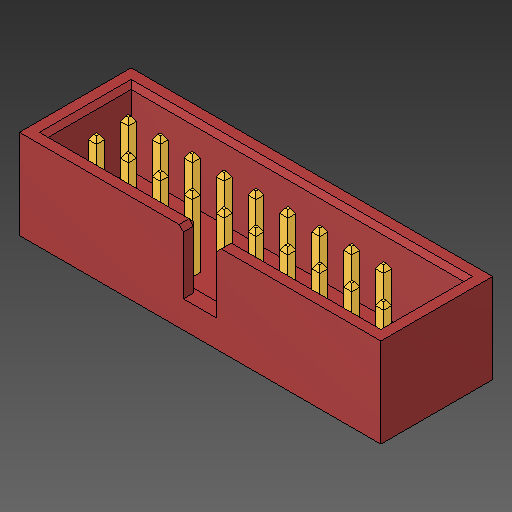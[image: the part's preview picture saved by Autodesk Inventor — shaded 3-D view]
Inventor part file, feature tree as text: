
AUTODESK INVENTOR PART (.ipt)
format: ipt  version: 2018.2 (Build 222227000, 227)  size: 210,432 bytes
history: native  units: mm
features: other x38, chamfer x2
ambient origin geometry x8: Origin, YZ Plane, XZ Plane, XY Plane, X Axis, Y Axis, Z Axis, Center Point
bodies: Body1 (feature_tree), Body2 (feature_tree), Body3 (feature_tree), Body4 (feature_tree), Body5 (feature_tree), Body6 (feature_tree), Body7 (feature_tree), Body8 (feature_tree), Body9 (feature_tree), Body10 (feature_tree), Body11 (feature_tree), Body12 (feature_tree), Body13 (feature_tree), Body14 (feature_tree), Body15 (feature_tree), Body16 (feature_tree), Body17 (feature_tree), Body18 (feature_tree), Body19 (feature_tree), Body20 (feature_tree)
feature tree (40):
  other  "ソリッド1"
  other  "ソリッド2"
  other  "ソリッド3"
  other  "ソリッド4"
  other  "ソリッド5"
  other  "ソリッド6"
  other  "ソリッド7"
  other  "ソリッド8"
  other  "ソリッド9"
  other  "ソリッド10"
  other  "ソリッド11"
  other  "ソリッド12"
  other  "ソリッド13"
  other  "ソリッド14"
  other  "ソリッド15"
  other  "ソリッド16"
  other  "ソリッド17"
  other  "ソリッド18"
  other  "ソリッド19"
  other  "ソリッド20"
  chamfer  "Chamfer1"  [1 undecoded]
  chamfer  "Chamfer2"  [1 undecoded]
  other  "LPattern3[1]"
  other  "LPattern3[2]"
  other  "LPattern3[3]"
  other  "LPattern3[4]"
  other  "LPattern3[5]"
  other  "LPattern3[6]"
  other  "LPattern3[7]"
  other  "LPattern3[8]"
  other  "LPattern3[9]"
  other  "LPattern3[10]"
  other  "LPattern3[11]"
  other  "LPattern3[12]"
  other  "LPattern3[13]"
  other  "LPattern3[14]"
  other  "LPattern3[15]"
  other  "LPattern3[16]"
  other  "LPattern3[17]"
  other  "LPattern3[18]"
note: 2 required parameter values undecoded (feature->parameter linkage not recoverable at this tier; creation-order binding heuristic only, values carry confidence <= 0.55)
